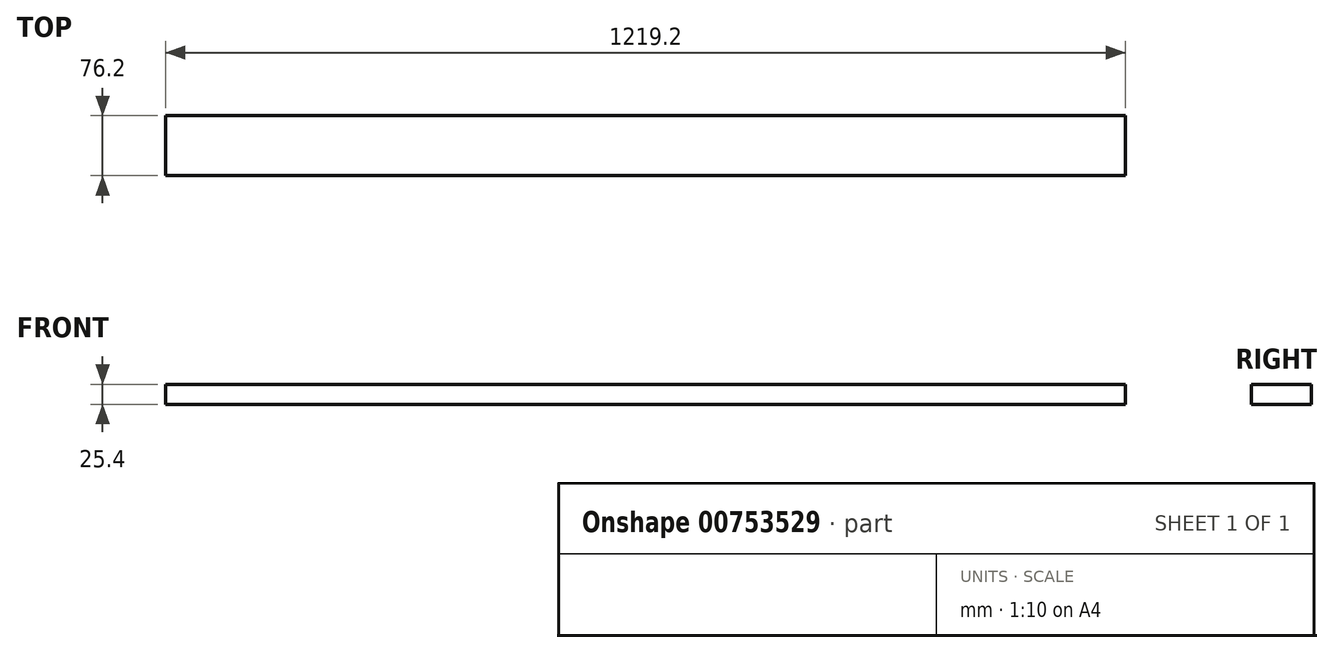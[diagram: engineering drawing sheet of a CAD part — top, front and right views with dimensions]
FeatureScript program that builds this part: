
annotation { "Feature Type Name" : "Feature", "Feature Type Description" : "" }
export const myFeature = defineFeature(function(context is Context, id is Id, definition is map)
    precondition{}
    {
        {
            var Q0;
            Q0=qCreatedBy(makeId("Top.planeOp"),FACE);
            var sketch = newSketch(context, id + "F0", { "sketchPlane" : qUnion([Q0])});
            skLineSegment(sketch, "E0.bottom", {"start": v(609.6, -38.1) * mm, "end": v(-609.6, -38.1) * mm});
            skLineSegment(sketch, "E0.top", {"start": v(609.6, 38.1) * mm, "end": v(-609.6, 38.1) * mm});
            skLineSegment(sketch, "E0.left", {"start": v(609.6, -38.1) * mm, "end": v(609.6, 38.1) * mm});
            skLineSegment(sketch, "E0.right", {"start": v(-609.6, -38.1) * mm, "end": v(-609.6, 38.1) * mm});
            skPoint(sketch, "E0.middle", {"position": v(0, 0) * mm});
            skSolve(sketch);
        }
        {
            var Q0;
            Q0=makeQuery(id+"F0.imprint","IMPRINT",FACE,{"disambiguationData":[TD([[makeQuery(id+"F0.imprint","IMPRINT",EDGE,{"derivedFrom":sQuery(id+"F0.wireOp",EDGE,"E0.bottom")}),-1.0]])]});
            extrude(context, id + "F1", {"entities" : qUnion([Q0]), "endBound" : BoundingType.SYMMETRIC, "depth" : 25.4 * mm, "offsetDistance" : 25.4 * mm});
        }
    });
